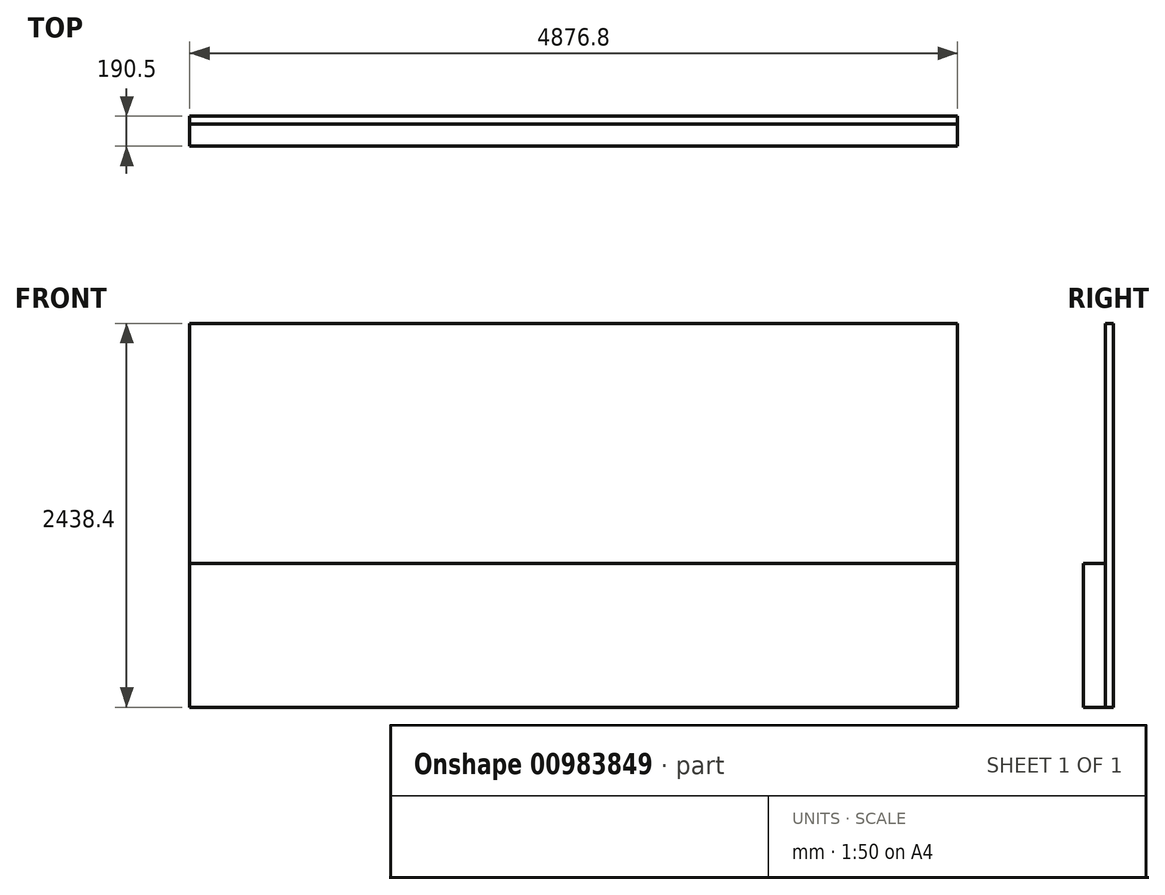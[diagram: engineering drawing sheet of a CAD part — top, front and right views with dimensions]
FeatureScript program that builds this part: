
annotation { "Feature Type Name" : "Feature", "Feature Type Description" : "" }
export const myFeature = defineFeature(function(context is Context, id is Id, definition is map)
    precondition{}
    {
        {
            var Q0;
            Q0=qCreatedBy(makeId("Front.planeOp"),FACE);
            var sketch = newSketch(context, id + "F0", { "sketchPlane" : qUnion([Q0])});
            skLineSegment(sketch, "E0.bottom", {"start": v(0, 0) * mm, "end": v(4876.8, 0) * mm});
            skLineSegment(sketch, "E0.top", {"start": v(0, 914.4) * mm, "end": v(4876.8, 914.4) * mm});
            skLineSegment(sketch, "E0.left", {"start": v(0, 0) * mm, "end": v(0, 914.4) * mm});
            skLineSegment(sketch, "E0.right", {"start": v(4876.8, 0) * mm, "end": v(4876.8, 914.4) * mm});
            skSolve(sketch);
        }
        {
            var Q0;
            Q0=makeQuery(id+"F0.imprint","IMPRINT",FACE,{"disambiguationData":[TD([[makeQuery(id+"F0.imprint","IMPRINT",EDGE,{"derivedFrom":sQuery(id+"F0.wireOp",EDGE,"E0.bottom")}),1.0]])]});
            extrude(context, id + "F1", {"entities" : qUnion([Q0]), "depth" : 139.7 * mm, "offsetDistance" : 25.4 * mm});
        }
        {
            var Q0;
            Q0=qCreatedBy(makeId("Front.planeOp"),FACE);
            var sketch = newSketch(context, id + "F2", { "sketchPlane" : qUnion([Q0])});
            skLineSegment(sketch, "E1.bottom", {"start": v(0, 0) * mm, "end": v(4876.8, 0) * mm});
            skLineSegment(sketch, "E1.top", {"start": v(0, 2438.4) * mm, "end": v(4876.8, 2438.4) * mm});
            skLineSegment(sketch, "E1.left", {"start": v(0, 0) * mm, "end": v(0, 2438.4) * mm});
            skLineSegment(sketch, "E1.right", {"start": v(4876.8, 0) * mm, "end": v(4876.8, 2438.4) * mm});
            skSolve(sketch);
        }
        {
            var Q0;
            Q0=makeQuery(id+"F2.imprint","IMPRINT",FACE,{"disambiguationData":[TD([[makeQuery(id+"F2.imprint","IMPRINT",EDGE,{"derivedFrom":sQuery(id+"F2.wireOp",EDGE,"E1.bottom")}),1.0]])]});
            extrude(context, id + "F3", {"entities" : qUnion([Q0]), "oppositeDirection" : true, "depth" : 50.8 * mm, "offsetDistance" : 25.4 * mm});
        }
    });
